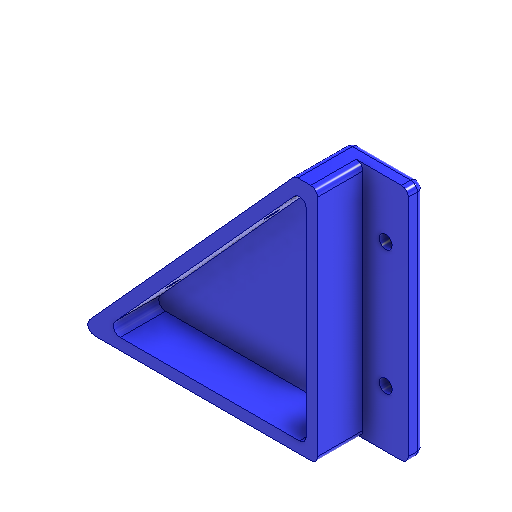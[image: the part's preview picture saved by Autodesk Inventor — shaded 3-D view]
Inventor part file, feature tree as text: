
AUTODESK INVENTOR PART (.ipt)
format: ipt  version: 2024.1 (Build 281209000, 209)  size: 155,648 bytes
history: native  units: in
note: dims shown in document units (in); Inventor stores cm internally (conversion verified against a paired STEP export)
features: other x3, sketch x3
ambient origin geometry x8: Origin, YZ Plane, XZ Plane, XY Plane, X Axis, Y Axis, Z Axis, Center Point
bodies: Solid1 (feature_tree)
feature tree (6):
  other  "Controls Support.ipt"
  other  "Solid1::Controls Support.ipt"
  other  "TaggingFeature1"
  sketch  "Sketch1"  dims[d0=0.3937in]
  sketch  "Sketch2"
  sketch  "Sketch3"
